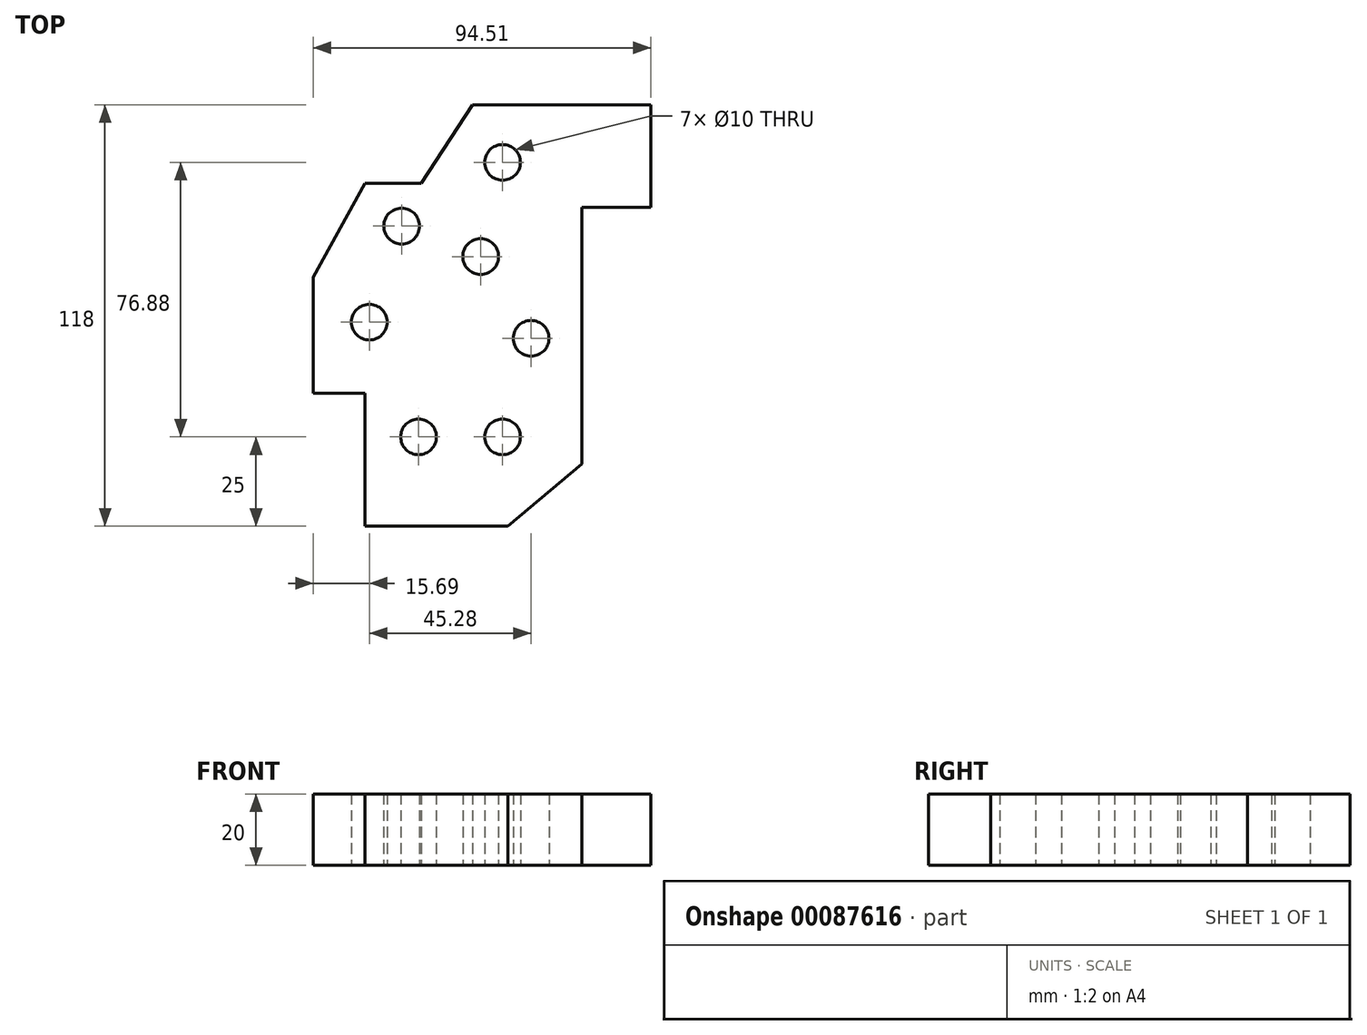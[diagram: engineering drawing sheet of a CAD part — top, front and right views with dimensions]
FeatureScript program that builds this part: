
annotation { "Feature Type Name" : "Feature", "Feature Type Description" : "" }
export const myFeature = defineFeature(function(context is Context, id is Id, definition is map)
    precondition{}
    {
        {
            var Q0;
            Q0=qCreatedBy(makeId("Top.planeOp"),FACE);
            var sketch = newSketch(context, id + "F0", { "sketchPlane" : qUnion([Q0])});
            skLineSegment(sketch, "E0", {"start": v(0, 0) * mm, "end": v(40, 0) * mm});
            skLineSegment(sketch, "E1", {"start": v(40, 0) * mm, "end": v(60.74, 17.4) * mm});
            skLineSegment(sketch, "E2", {"start": v(60.74, 17.4) * mm, "end": v(60.74, 89.33) * mm});
            skLineSegment(sketch, "E3", {"start": v(60.74, 89.33) * mm, "end": v(80.04, 89.33) * mm});
            skLineSegment(sketch, "E4", {"start": v(80.04, 89.33) * mm, "end": v(80.04, 118) * mm});
            skLineSegment(sketch, "E5", {"start": v(80.04, 118) * mm, "end": v(30.04, 118) * mm});
            skLineSegment(sketch, "E6", {"start": v(30.04, 118) * mm, "end": v(15.8, 96.07) * mm});
            skLineSegment(sketch, "E7", {"start": v(15.8, 96.07) * mm, "end": v(0, 96.07) * mm});
            skLineSegment(sketch, "E8", {"start": v(0, 96.07) * mm, "end": v(-14.47, 69.75) * mm});
            skLineSegment(sketch, "E9", {"start": v(-14.47, 69.75) * mm, "end": v(-14.47, 37.28) * mm});
            skLineSegment(sketch, "E10", {"start": v(-14.47, 37.28) * mm, "end": v(0, 37.28) * mm});
            skLineSegment(sketch, "E11", {"start": v(0, 37.28) * mm, "end": v(0, 0) * mm});
            skSolve(sketch);
        }
        {
            var Q0;
            Q0 = qSketchRegion(id + "F0", true);
            extrude(context, id + "F1", {"entities" : qUnion([Q0]), "depth" : 20 * mm});
        }
        {
            var Q0;
            Q0=qCreatedBy(makeId("Top.planeOp"),FACE);
            var sketch = newSketch(context, id + "F2", { "sketchPlane" : qUnion([Q0])});
            skCircle(sketch, "E12", {"center": v(15, 25) * mm, "radius": 5 * mm});
            skCircle(sketch, "E13", {"center": v(38.5, 25) * mm, "radius": 5 * mm});
            skCircle(sketch, "E14", {"center": v(46.5, 52.61) * mm, "radius": 5 * mm});
            skCircle(sketch, "E15", {"center": v(1.22, 57.14) * mm, "radius": 5 * mm});
            skCircle(sketch, "E16", {"center": v(32.38, 75.51) * mm, "radius": 5 * mm});
            skCircle(sketch, "E17", {"center": v(10.27, 84.04) * mm, "radius": 5 * mm});
            skCircle(sketch, "E18", {"center": v(38.5, 101.88) * mm, "radius": 5 * mm});
            skLineSegment(sketch, "E19", {"start": v(15, 25) * mm, "end": v(38.5, 25) * mm, "construction": true});
            skLineSegment(sketch, "E20", {"start": v(38.5, 25) * mm, "end": v(38.5, 101.88) * mm, "construction": true});
            skSolve(sketch);
        }
        {
            var Q0;
            Q0 = qSketchRegion(id + "F2", true);
            extrude(context, id + "F3", {"entities" : qUnion([Q0]), "operationType" : NewBodyOperationType.REMOVE, "endBound" : BoundingType.THROUGH_ALL, "depth" : 25 * mm});
        }
    });
